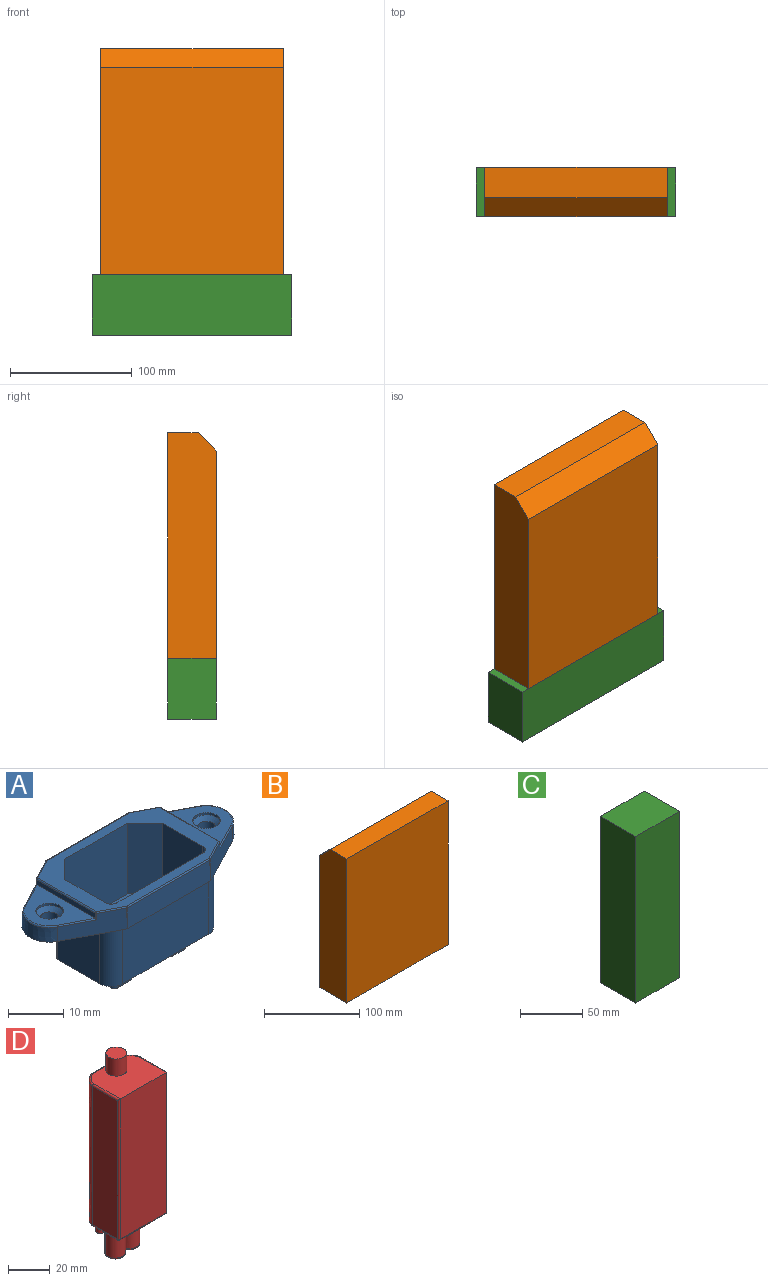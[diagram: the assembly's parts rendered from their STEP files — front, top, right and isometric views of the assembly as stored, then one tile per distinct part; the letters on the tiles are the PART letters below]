
ASSEMBLY  parts=4 mates=2
PART A: 313 faces, bbox 50.8x21.1x21.2 mm
  f0: plane 28x19.35mm, normal (0,0,-1), area 388.7mm2, adj f9,f10,f11,f12,f13,f14,f34,f35
  f1: plane 31.25x20.29mm, normal (0,0,1), area 219.7mm2, adj f15,f16,f17,f18,f19,f20,f50,f51
  f2: plane 11.73x6.18mm, normal (0.46,0.89,0.03), area 48.9mm2, adj f3,f52,f65,f67,f72,f73
  f3: cone r=5mm half-angle=2deg, axis (0,0,-1), area 33.6mm2, adj f2,f4,f52,f66
  f4: plane 11.73x6.18mm, normal (0.46,-0.89,0.03), area 48.9mm2, adj f3,f52,f68,f71,f76,f77
  f5: plane 11.73x6.18mm, normal (-0.46,-0.89,0.03), area 48.9mm2, adj f6,f52,f83,f88,f92,f94
  f6: cone r=5mm half-angle=2deg, axis (0,0,-1), area 33.6mm2, adj f5,f7,f52,f93
  f7: plane 11.73x6.18mm, normal (-0.46,0.89,0.03), area 48.9mm2, adj f6,f52,f78,f84,f89,f91
  f8: plane 25x16.35mm, normal (0,0,1), area 365.3mm2, adj f15,f16,f17,f18,f19,f20,f21,f22
  f9: plane 16.83x12.45mm, normal (0,1,0), area 209.5mm2, adj f0,f52,f108,f109
  f10: plane 12.45x5.09mm, normal (0.71,0.71,0), area 89.5mm2, adj f0,f52,f107,f108
  f11: plane 12.45x10.76mm, normal (1,0,0), area 134mm2, adj f0,f49,f52,f107
  f12: plane 22x12.45mm, normal (0,-1,0), area 273.9mm2, adj f0,f48,f49,f52
  f13: plane 12.45x10.76mm, normal (-1,0,0), area 134mm2, adj f0,f48,f52,f110
  f14: plane 12.45x5.09mm, normal (-0.71,0.71,0), area 89.5mm2, adj f0,f52,f109,f110
  f15: plane 16x15.7mm, normal (0,-1,0), area 251.2mm2, adj f1,f8,f16,f20
  f16: plane 15.7x4.5mm, normal (-0.71,-0.71,0), area 99.9mm2, adj f1,f8,f15,f17
  f17: plane 15.7x10.35mm, normal (-1,0,0), area 162.5mm2, adj f1,f8,f16,f50
  f18: plane 22x15.7mm, normal (0,1,0), area 345.4mm2, adj f1,f8,f50,f51
  f19: plane 15.7x10.35mm, normal (1,0,0), area 162.5mm2, adj f1,f8,f20,f51
  f20: plane 15.7x4.5mm, normal (0.71,-0.71,0), area 99.9mm2, adj f1,f8,f15,f19
  f21: plane 5.5x3.9mm, normal (1,0,0), area 21.5mm2, adj f8,f22,f24,f33
  f22: plane 5.5x1.9mm, normal (0,-1,0), area 10.5mm2, adj f8,f21,f23,f33
  f23: plane 5.5x3.9mm, normal (-1,0,0), area 21.5mm2, adj f8,f22,f24,f33
  f24: plane 5.5x1.9mm, normal (0,1,0), area 10.5mm2, adj f8,f21,f23,f33
  f25: plane 5.5x3.9mm, normal (1,0,0), area 21.5mm2, adj f8,f26,f28,f38
  f26: plane 5.5x1.9mm, normal (0,-1,0), area 10.5mm2, adj f8,f25,f27,f38
  f27: plane 5.5x3.9mm, normal (-1,0,0), area 21.5mm2, adj f8,f26,f28,f38
  f28: plane 5.5x1.9mm, normal (0,1,0), area 10.5mm2, adj f8,f25,f27,f38
  f29: plane 5.5x3.9mm, normal (1,0,0), area 21.5mm2, adj f8,f30,f32,f43
  f30: plane 5.5x1.9mm, normal (0,-1,0), area 10.5mm2, adj f8,f29,f31,f43
  f31: plane 5.5x3.9mm, normal (-1,0,0), area 21.5mm2, adj f8,f30,f32,f43
  f32: plane 5.5x1.9mm, normal (0,1,0), area 10.5mm2, adj f8,f29,f31,f43
  f33: plane 6.9x4.9mm, normal (0,0,-1), area 25.5mm2, adj f21,f22,f23,f24,f34,f35,f36,f37
  f34: plane 4.9x4mm, normal (1,0,0), area 19.6mm2, adj f0,f33,f95,f98
  f35: plane 4x2.9mm, normal (0,-1,0), area 11.6mm2, adj f0,f33,f95,f96
  f36: plane 4.9x4mm, normal (-1,0,0), area 19.6mm2, adj f0,f33,f96,f97
  f37: plane 4x2.9mm, normal (0,1,0), area 11.6mm2, adj f0,f33,f97,f98
  f38: plane 6.9x4.9mm, normal (0,0,-1), area 25.5mm2, adj f25,f26,f27,f28,f39,f40,f41,f42
  f39: plane 4x2.9mm, normal (0,-1,0), area 11.6mm2, adj f0,f38,f99,f102
  f40: plane 4.9x4mm, normal (-1,0,0), area 19.6mm2, adj f0,f38,f99,f100
  f41: plane 4x2.9mm, normal (0,1,0), area 11.6mm2, adj f0,f38,f100,f101
  f42: plane 4.9x4mm, normal (1,0,0), area 19.6mm2, adj f0,f38,f101,f102
  f43: plane 6.9x4.9mm, normal (0,0,-1), area 25.5mm2, adj f29,f30,f31,f32,f44,f45,f46,f47
  f44: plane 4.9x4mm, normal (1,0,0), area 19.6mm2, adj f0,f43,f104,f105
  f45: plane 4x2.9mm, normal (0,-1,0), area 11.6mm2, adj f0,f43,f103,f104
  f46: plane 4.9x4mm, normal (-1,0,0), area 19.6mm2, adj f0,f43,f103,f106
  f47: plane 4x2.9mm, normal (0,1,0), area 11.6mm2, adj f0,f43,f105,f106
  f48: cylinder r=3mm len=12.45mm, axis (0,0,1), area 58.7mm2, adj f0,f12,f13,f52
  f49: cylinder r=3mm len=12.45mm, axis (0,0,1), area 58.7mm2, adj f0,f11,f12,f52
  f50: cylinder r=1.5mm len=15.7mm, axis (0,0,-1), area 37mm2, adj f1,f8,f17,f18
  f51: cylinder r=1.5mm len=15.7mm, axis (0,0,-1), area 37mm2, adj f1,f8,f18,f19
  f52: plane 50.2x21.1mm, normal (0,0,-1), area 310mm2, adj f2,f3,f4,f5,f6,f7,f9,f10
  f53: plane 21.2x4.51mm, normal (0,1,0.03), area 95.5mm2, adj f52,f72,f78,f79
  f54: plane 21.2x4.51mm, normal (0,-1,0.03), area 95.5mm2, adj f52,f77,f82,f83
  f55: plane 15.11x1.18mm, normal (-1,0,0), area 17.3mm2, adj f56,f87,f89,f91,f92,f94
  f56: plane 14.86x8.87mm, normal (0,0,1), area 68.6mm2, adj f55,f64,f91,f93,f94
  f57: plane 14.86x8.87mm, normal (0,0,1), area 68.6mm2, adj f58,f61,f65,f66,f68
  f58: plane 15.11x1.18mm, normal (1,0,0), area 17.3mm2, adj f57,f65,f67,f68,f70,f71
  f59: cylinder r=1.65mm len=3.3mm, axis (0,0,1), area 20.7mm2, adj f52,f60
  f60: cone r=2.5mm half-angle=45deg, axis (0,0,1), area 15.7mm2, adj f59,f61
  f61: cylinder r=2.5mm len=5mm, axis (0,0,1), area 7.9mm2, adj f57,f60
  f62: cylinder r=1.65mm len=3.3mm, axis (0,0,1), area 20.7mm2, adj f52,f63
  f63: cone r=2.5mm half-angle=45deg, axis (0,0,1), area 15.7mm2, adj f62,f64
  f64: cylinder r=2.5mm len=5mm, axis (0,0,1), area 7.9mm2, adj f56,f63
  f65: cylinder r=0.25mm len=6.73mm, axis (0.89,-0.46,0), area 2.8mm2, adj f2,f57,f58,f66,f67
  f66: torus R=4.64mm, axis (0,0,1), area 4mm2, adj f3,f57,f65,f68
  f67: cylinder r=0.25mm len=1.41mm, axis (0,0.04,-1), area 0.3mm2, adj f2,f58,f65,f69
  f68: cylinder r=0.25mm len=6.73mm, axis (-0.89,-0.46,0), area 2.8mm2, adj f4,f57,f58,f66,f71
  f69: sphere r=0.25mm, area 0.1mm2, adj f67,f70,f73
  f70: cylinder r=0.25mm len=15.01mm, axis (0,1,0), area 5.9mm2, adj f1,f58,f69,f74
  f71: cylinder r=0.25mm len=1.41mm, axis (0,0.04,1), area 0.3mm2, adj f4,f58,f68,f74
  f72: cylinder r=0.25mm len=4.51mm, axis (-0.01,-0.03,1), area 0.5mm2, adj f2,f52,f53,f75
  f73: cylinder r=0.25mm len=5.18mm, axis (-0.89,0.46,0), area 2.2mm2, adj f1,f2,f69,f75
  f74: sphere r=0.25mm, area 0.1mm2, adj f70,f71,f76
  f75: sphere r=0.25mm, area 0mm2, adj f72,f73,f79
  f76: cylinder r=0.25mm len=5.18mm, axis (0.89,0.46,0), area 2.2mm2, adj f1,f4,f74,f80
  f77: cylinder r=0.25mm len=4.51mm, axis (-0.01,0.03,1), area 0.5mm2, adj f4,f52,f54,f80
  f78: cylinder r=0.25mm len=4.51mm, axis (0.01,-0.03,1), area 0.5mm2, adj f7,f52,f53,f81
  f79: cylinder r=0.25mm len=21.12mm, axis (-1,0,0), area 8.1mm2, adj f1,f53,f75,f81
  f80: sphere r=0.25mm, area 0mm2, adj f76,f77,f82
  f81: sphere r=0.25mm, area 0mm2, adj f78,f79,f84
  f82: cylinder r=0.25mm len=21.12mm, axis (1,0,0), area 8.1mm2, adj f1,f54,f80,f85
  f83: cylinder r=0.25mm len=4.51mm, axis (0.01,0.03,1), area 0.5mm2, adj f5,f52,f54,f85
  f84: cylinder r=0.25mm len=5.18mm, axis (-0.89,-0.46,0), area 2.2mm2, adj f1,f7,f81,f86
  f85: sphere r=0.25mm, area 0mm2, adj f82,f83,f88
  f86: sphere r=0.25mm, area 0.1mm2, adj f84,f87,f89
  f87: cylinder r=0.25mm len=15.01mm, axis (0,-1,0), area 5.9mm2, adj f1,f55,f86,f90
  f88: cylinder r=0.25mm len=5.18mm, axis (0.89,-0.46,0), area 2.2mm2, adj f1,f5,f85,f90
  f89: cylinder r=0.25mm len=1.41mm, axis (0,-0.04,1), area 0.3mm2, adj f7,f55,f86,f91
  f90: sphere r=0.25mm, area 0.1mm2, adj f87,f88,f92
  f91: cylinder r=0.25mm len=6.73mm, axis (0.89,0.46,0), area 2.8mm2, adj f7,f55,f56,f89,f93
  f92: cylinder r=0.25mm len=1.41mm, axis (0,-0.04,-1), area 0.3mm2, adj f5,f55,f90,f94
  f93: torus R=4.64mm, axis (0,0,1), area 4mm2, adj f6,f56,f91,f94
  f94: cylinder r=0.25mm len=6.73mm, axis (-0.89,0.46,0), area 2.8mm2, adj f5,f55,f56,f92,f93
  f95: cylinder r=1mm len=4mm, axis (0,0,1), area 6.3mm2, adj f0,f33,f34,f35
  f96: cylinder r=1mm len=4mm, axis (0,0,1), area 6.3mm2, adj f0,f33,f35,f36
  f97: cylinder r=1mm len=4mm, axis (0,0,1), area 6.3mm2, adj f0,f33,f36,f37
  f98: cylinder r=1mm len=4mm, axis (0,0,1), area 6.3mm2, adj f0,f33,f34,f37
  f99: cylinder r=1mm len=4mm, axis (0,0,1), area 6.3mm2, adj f0,f38,f39,f40
  f100: cylinder r=1mm len=4mm, axis (0,0,1), area 6.3mm2, adj f0,f38,f40,f41
  f101: cylinder r=1mm len=4mm, axis (0,0,1), area 6.3mm2, adj f0,f38,f41,f42
  f102: cylinder r=1mm len=4mm, axis (0,0,1), area 6.3mm2, adj f0,f38,f39,f42
  f103: cylinder r=1mm len=4mm, axis (0,0,1), area 6.3mm2, adj f0,f43,f45,f46
  f104: cylinder r=1mm len=4mm, axis (0,0,1), area 6.3mm2, adj f0,f43,f44,f45
  f105: cylinder r=1mm len=4mm, axis (0,0,1), area 6.3mm2, adj f0,f43,f44,f47
  f106: cylinder r=1mm len=4mm, axis (0,0,1), area 6.3mm2, adj f0,f43,f46,f47
  f107: cylinder r=0.5mm len=12.45mm, axis (0,0,1), area 4.9mm2, adj f0,f10,f11,f52
  f108: cylinder r=0.5mm len=12.45mm, axis (0,0,1), area 4.9mm2, adj f0,f9,f10,f52
  f109: cylinder r=0.5mm len=12.45mm, axis (0,0,1), area 4.9mm2, adj f0,f9,f14,f52
  f110: cylinder r=0.5mm len=12.45mm, axis (0,0,1), area 4.9mm2, adj f0,f13,f14,f52
  f111: plane 2x0.2mm, normal (-1,0,0), area 0.4mm2, adj f0,f112,f117,f118
  f112: plane 0.2x0.17mm, normal (0,1,0), area 0mm2, adj f0,f111,f113,f118
  f113: extruded ~0.55x0.5mm, area 0.2mm2, adj f0,f112,f114,f118
  f114: plane 0.24x0.2mm, normal (1,0,0), area 0mm2, adj f0,f113,f115,f118
  f115: extruded ~0.46x0.3mm, area 0.1mm2, adj f0,f114,f116,f118
  f116: plane 1.56x0.2mm, normal (1,0,0), area 0.3mm2, adj f0,f115,f117,f118
  f117: plane 0.26x0.2mm, normal (0,-1,0), area 0.1mm2, adj f0,f111,f116,f118
  f118: plane 2x0.72mm, normal (0,0,-1), area 0.6mm2, adj f111,f112,f113,f114,f115,f116,f117
  f119: plane 2.03x1.28mm, normal (0,0,-1), area 1.2mm2, adj f120,f121,f122,f123,f124,f125,f126,f127
  f120: extruded ~0.82x0.2mm, area 0.2mm2, adj f0,f119,f121,f124
  f121: extruded ~0.45x0.2mm, area 0.1mm2, adj f0,f119,f120,f122
  f122: extruded ~1.01x0.64mm, area 0.3mm2, adj f0,f119,f121,f123
  f123: extruded ~1.01x0.64mm, area 0.3mm2, adj f0,f119,f122,f124
  f124: extruded ~1.01x0.64mm, area 0.3mm2, adj f0,f119,f120,f123
  f125: extruded ~0.65x0.2mm, area 0.1mm2, adj f119,f126,f129,f130
  f126: extruded ~0.78x0.38mm, area 0.2mm2, adj f119,f125,f127,f130
  f127: extruded ~0.78x0.38mm, area 0.2mm2, adj f119,f126,f128,f130
  f128: extruded ~0.78x0.39mm, area 0.2mm2, adj f119,f127,f129,f130
  f129: extruded ~0.27x0.2mm, area 0.1mm2, adj f119,f125,f128,f130
  f130: plane 1.56x0.77mm, normal (0,0,-1), area 1mm2, adj f125,f126,f127,f128,f129
  f131: plane 2x1.91mm, normal (0,0,-1), area 1.2mm2, adj f132,f133,f134,f135,f136,f137,f138,f139
  f132: plane 0.3x0.2mm, normal (0,-1,0), area 0.1mm2, adj f0,f131,f133,f139
  f133: plane 0.62x0.23mm, normal (-0.94,-0.35,0), area 0.1mm2, adj f0,f131,f132,f134
  f134: plane 0.85x0.2mm, normal (0,-1,0), area 0.2mm2, adj f0,f131,f133,f135
  f135: plane 0.62x0.23mm, normal (0.94,-0.35,0), area 0.1mm2, adj f0,f131,f134,f136
  f136: plane 0.3x0.2mm, normal (0,-1,0), area 0.1mm2, adj f0,f131,f135,f137
  f137: plane 2x0.79mm, normal (-0.93,0.37,0), area 0.4mm2, adj f0,f131,f136,f138
  f138: plane 0.32x0.2mm, normal (0,1,0), area 0.1mm2, adj f0,f131,f137,f139
  f139: plane 2x0.79mm, normal (0.93,0.37,0), area 0.4mm2, adj f0,f131,f132,f138
  f140: plane 0.55x0.2mm, normal (-0.94,-0.35,0), area 0.1mm2, adj f131,f141,f144,f145
  f141: plane 0.68x0.2mm, normal (0,1,0), area 0.1mm2, adj f131,f140,f142,f145
  f142: plane 0.53x0.2mm, normal (0.94,-0.35,0), area 0.1mm2, adj f131,f141,f143,f145
  f143: extruded ~0.4x0.2mm, area 0.1mm2, adj f131,f142,f144,f145
  f144: extruded ~0.37x0.2mm, area 0.1mm2, adj f131,f140,f143,f145
  f145: plane 0.92x0.68mm, normal (0,0,-1), area 0.3mm2, adj f140,f141,f142,f143,f144
  f146: extruded ~0.35x0.23mm, area 0.1mm2, adj f0,f147,f154,f155
  f147: extruded ~0.66x0.23mm, area 0.1mm2, adj f0,f146,f148,f155
  f148: extruded ~0.38x0.23mm, area 0.1mm2, adj f0,f147,f149,f155
  f149: plane 0.28x0.2mm, normal (-1,0,0), area 0.1mm2, adj f0,f148,f150,f155
  f150: extruded ~0.35x0.23mm, area 0.1mm2, adj f0,f149,f151,f155
  f151: extruded ~0.23x0.2mm, area 0.1mm2, adj f0,f150,f152,f155
  f152: extruded ~0.43x0.2mm, area 0.1mm2, adj f0,f151,f153,f155
  f153: extruded ~0.38x0.23mm, area 0.1mm2, adj f0,f152,f154,f155
  f154: plane 0.28x0.2mm, normal (1,0,0), area 0.1mm2, adj f0,f146,f153,f155
  f155: plane 1.38x0.51mm, normal (0,0,-1), area 0.4mm2, adj f146,f147,f148,f149,f150,f151,f152,f153
  f156: plane 2x0.2mm, normal (-1,0,0), area 0.4mm2, adj f0,f157,f162,f163
  f157: plane 0.2x0.17mm, normal (0,1,0), area 0mm2, adj f0,f156,f158,f163
  f158: extruded ~0.55x0.5mm, area 0.2mm2, adj f0,f157,f159,f163
  f159: plane 0.24x0.2mm, normal (1,0,0), area 0mm2, adj f0,f158,f160,f163
  f160: extruded ~0.46x0.3mm, area 0.1mm2, adj f0,f159,f161,f163
  f161: plane 1.56x0.2mm, normal (1,0,0), area 0.3mm2, adj f0,f160,f162,f163
  f162: plane 0.26x0.2mm, normal (0,-1,0), area 0.1mm2, adj f0,f156,f161,f163
  f163: plane 2x0.72mm, normal (0,0,-1), area 0.6mm2, adj f156,f157,f158,f159,f160,f161,f162
  f164: extruded ~0.62x0.56mm, area 0.2mm2, adj f0,f165,f179,f180
  f165: extruded ~0.51x0.24mm, area 0.1mm2, adj f0,f164,f166,f180
  f166: extruded ~0.47x0.2mm, area 0.1mm2, adj f0,f165,f167,f180
  f167: extruded ~0.65x0.59mm, area 0.2mm2, adj f0,f166,f168,f180
  f168: extruded ~0.36x0.2mm, area 0.1mm2, adj f0,f167,f169,f180
  f169: plane 0.52x0.2mm, normal (-0.98,-0.19,0), area 0.1mm2, adj f0,f168,f170,f180
  f170: plane 0.74x0.2mm, normal (0,-1,0), area 0.1mm2, adj f0,f169,f171,f180
  f171: plane 0.26x0.2mm, normal (-1,0,0), area 0.1mm2, adj f0,f170,f172,f180
  f172: plane 0.95x0.2mm, normal (0,1,0), area 0.2mm2, adj f0,f171,f173,f180
  f173: plane 1.03x0.21mm, normal (0.98,0.2,0), area 0.2mm2, adj f0,f172,f174,f180
  f174: plane 0.26x0.2mm, normal (0.1,-1,0), area 0.1mm2, adj f0,f173,f175,f180
  f175: extruded ~0.34x0.2mm, area 0.1mm2, adj f0,f174,f176,f180
  f176: extruded ~0.43x0.4mm, area 0.1mm2, adj f0,f175,f177,f180
  f177: extruded ~0.47x0.4mm, area 0.1mm2, adj f0,f176,f178,f180
  f178: extruded ~0.37x0.36mm, area 0.1mm2, adj f0,f177,f179,f180
  f179: plane 0.26x0.2mm, normal (0.1,1,0), area 0.1mm2, adj f0,f164,f178,f180
  f180: plane 2x1.28mm, normal (0,0,-1), area 1.1mm2, adj f164,f165,f166,f167,f168,f169,f170,f171
  f181: plane 2x1.91mm, normal (0,0,-1), area 1.2mm2, adj f182,f183,f184,f185,f186,f187,f188,f189
  f182: plane 0.3x0.2mm, normal (0,-1,0), area 0.1mm2, adj f0,f181,f183,f189
  f183: plane 0.62x0.23mm, normal (-0.94,-0.35,0), area 0.1mm2, adj f0,f181,f182,f184
  f184: plane 0.85x0.2mm, normal (0,-1,0), area 0.2mm2, adj f0,f181,f183,f185
  f185: plane 0.62x0.23mm, normal (0.94,-0.35,0), area 0.1mm2, adj f0,f181,f184,f186
  f186: plane 0.3x0.2mm, normal (0,-1,0), area 0.1mm2, adj f0,f181,f185,f187
  f187: plane 2x0.79mm, normal (-0.93,0.37,0), area 0.4mm2, adj f0,f181,f186,f188
  f188: plane 0.32x0.2mm, normal (0,1,0), area 0.1mm2, adj f0,f181,f187,f189
  f189: plane 2x0.79mm, normal (0.93,0.37,0), area 0.4mm2, adj f0,f181,f182,f188
  f190: plane 0.55x0.2mm, normal (-0.94,-0.35,0), area 0.1mm2, adj f181,f191,f194,f195
  f191: plane 0.68x0.2mm, normal (0,1,0), area 0.1mm2, adj f181,f190,f192,f195
  f192: plane 0.53x0.2mm, normal (0.94,-0.35,0), area 0.1mm2, adj f181,f191,f193,f195
  f193: extruded ~0.4x0.2mm, area 0.1mm2, adj f181,f192,f194,f195
  f194: extruded ~0.37x0.2mm, area 0.1mm2, adj f181,f190,f193,f195
  f195: plane 0.92x0.68mm, normal (0,0,-1), area 0.3mm2, adj f190,f191,f192,f193,f194
  f196: plane 2x0.2mm, normal (-1,0,0), area 0.4mm2, adj f0,f197,f202,f203
  f197: plane 0.2x0.17mm, normal (0,1,0), area 0mm2, adj f0,f196,f198,f203
  f198: extruded ~0.55x0.5mm, area 0.2mm2, adj f0,f197,f199,f203
  f199: plane 0.24x0.2mm, normal (1,0,0), area 0mm2, adj f0,f198,f200,f203
  f200: extruded ~0.46x0.3mm, area 0.1mm2, adj f0,f199,f201,f203
  f201: plane 1.56x0.2mm, normal (1,0,0), area 0.3mm2, adj f0,f200,f202,f203
  f202: plane 0.26x0.2mm, normal (0,-1,0), area 0.1mm2, adj f0,f196,f201,f203
  f203: plane 2x0.72mm, normal (0,0,-1), area 0.6mm2, adj f196,f197,f198,f199,f200,f201,f202
  f204: plane 2.03x1.28mm, normal (0,0,-1), area 1.2mm2, adj f205,f206,f207,f208,f209,f210,f211,f212
  f205: extruded ~0.82x0.2mm, area 0.2mm2, adj f0,f204,f206,f209
  f206: extruded ~0.45x0.2mm, area 0.1mm2, adj f0,f204,f205,f207
  f207: extruded ~1.01x0.64mm, area 0.3mm2, adj f0,f204,f206,f208
  f208: extruded ~1.01x0.64mm, area 0.3mm2, adj f0,f204,f207,f209
  f209: extruded ~1.01x0.64mm, area 0.3mm2, adj f0,f204,f205,f208
  f210: extruded ~0.65x0.2mm, area 0.1mm2, adj f204,f211,f214,f215
  f211: extruded ~0.78x0.38mm, area 0.2mm2, adj f204,f210,f212,f215
  f212: extruded ~0.78x0.38mm, area 0.2mm2, adj f204,f211,f213,f215
  f213: extruded ~0.78x0.39mm, area 0.2mm2, adj f204,f212,f214,f215
  f214: extruded ~0.27x0.2mm, area 0.1mm2, adj f204,f210,f213,f215
  f215: plane 1.56x0.77mm, normal (0,0,-1), area 1mm2, adj f210,f211,f212,f213,f214
  f216: plane 2x1.91mm, normal (0,0,-1), area 1.2mm2, adj f217,f218,f219,f220,f221,f222,f223,f224
  f217: plane 0.3x0.2mm, normal (0,-1,0), area 0.1mm2, adj f0,f216,f218,f224
  f218: plane 0.62x0.23mm, normal (-0.94,-0.35,0), area 0.1mm2, adj f0,f216,f217,f219
  f219: plane 0.85x0.2mm, normal (0,-1,0), area 0.2mm2, adj f0,f216,f218,f220
  f220: plane 0.62x0.23mm, normal (0.94,-0.35,0), area 0.1mm2, adj f0,f216,f219,f221
  f221: plane 0.3x0.2mm, normal (0,-1,0), area 0.1mm2, adj f0,f216,f220,f222
  f222: plane 2x0.79mm, normal (-0.93,0.37,0), area 0.4mm2, adj f0,f216,f221,f223
  f223: plane 0.32x0.2mm, normal (0,1,0), area 0.1mm2, adj f0,f216,f222,f224
  f224: plane 2x0.79mm, normal (0.93,0.37,0), area 0.4mm2, adj f0,f216,f217,f223
  f225: plane 0.55x0.2mm, normal (-0.94,-0.35,0), area 0.1mm2, adj f216,f226,f229,f230
  f226: plane 0.68x0.2mm, normal (0,1,0), area 0.1mm2, adj f216,f225,f227,f230
  f227: plane 0.53x0.2mm, normal (0.94,-0.35,0), area 0.1mm2, adj f216,f226,f228,f230
  f228: extruded ~0.4x0.2mm, area 0.1mm2, adj f216,f227,f229,f230
  f229: extruded ~0.37x0.2mm, area 0.1mm2, adj f216,f225,f228,f230
  f230: plane 0.92x0.68mm, normal (0,0,-1), area 0.3mm2, adj f225,f226,f227,f228,f229
  f231: plane 0.98x0.2mm, normal (0,1,0), area 0.2mm2, adj f0,f232,f243,f244
  f232: extruded ~0.4x0.37mm, area 0.1mm2, adj f0,f231,f233,f244
  f233: extruded ~0.82x0.56mm, area 0.2mm2, adj f0,f232,f234,f244
  f234: extruded ~0.62x0.55mm, area 0.2mm2, adj f0,f233,f235,f244
  f235: extruded ~0.64x0.56mm, area 0.2mm2, adj f0,f234,f236,f244
  f236: plane 0.26x0.2mm, normal (0.1,-1,0), area 0.1mm2, adj f0,f235,f237,f244
  f237: extruded ~0.38x0.36mm, area 0.1mm2, adj f0,f236,f238,f244
  f238: extruded ~0.36x0.32mm, area 0.1mm2, adj f0,f237,f239,f244
  f239: extruded ~0.7x0.54mm, area 0.2mm2, adj f0,f238,f240,f244
  f240: extruded ~0.57x0.46mm, area 0.1mm2, adj f0,f239,f241,f244
  f241: extruded ~0.2x0.18mm, area 0mm2, adj f0,f240,f242,f244
  f242: plane 1.31x0.2mm, normal (0,-1,0), area 0.3mm2, adj f0,f241,f243,f244
  f243: plane 0.26x0.2mm, normal (-1,0,0), area 0.1mm2, adj f0,f231,f242,f244
  f244: plane 2x1.31mm, normal (0,0,-1), area 1.1mm2, adj f231,f232,f233,f234,f235,f236,f237,f238
  f245: extruded ~0.62x0.56mm, area 0.2mm2, adj f0,f246,f260,f261
  f246: extruded ~0.51x0.24mm, area 0.1mm2, adj f0,f245,f247,f261
  f247: extruded ~0.47x0.2mm, area 0.1mm2, adj f0,f246,f248,f261
  f248: extruded ~0.65x0.59mm, area 0.2mm2, adj f0,f247,f249,f261
  f249: extruded ~0.36x0.2mm, area 0.1mm2, adj f0,f248,f250,f261
  f250: plane 0.52x0.2mm, normal (-0.98,-0.19,0), area 0.1mm2, adj f0,f249,f251,f261
  f251: plane 0.74x0.2mm, normal (0,-1,0), area 0.1mm2, adj f0,f250,f252,f261
  f252: plane 0.26x0.2mm, normal (-1,0,0), area 0.1mm2, adj f0,f251,f253,f261
  f253: plane 0.95x0.2mm, normal (0,1,0), area 0.2mm2, adj f0,f252,f254,f261
  f254: plane 1.03x0.21mm, normal (0.98,0.2,0), area 0.2mm2, adj f0,f253,f255,f261
  f255: plane 0.26x0.2mm, normal (0.1,-1,0), area 0.1mm2, adj f0,f254,f256,f261
  f256: extruded ~0.34x0.2mm, area 0.1mm2, adj f0,f255,f257,f261
  f257: extruded ~0.43x0.4mm, area 0.1mm2, adj f0,f256,f258,f261
  f258: extruded ~0.47x0.4mm, area 0.1mm2, adj f0,f257,f259,f261
  f259: extruded ~0.37x0.36mm, area 0.1mm2, adj f0,f258,f260,f261
  f260: plane 0.26x0.2mm, normal (0.1,1,0), area 0.1mm2, adj f0,f245,f259,f261
  f261: plane 2x1.28mm, normal (0,0,-1), area 1.1mm2, adj f245,f246,f247,f248,f249,f250,f251,f252
  f262: plane 2.03x1.28mm, normal (0,0,-1), area 1.2mm2, adj f263,f264,f265,f266,f267,f268,f269,f270
  f263: extruded ~0.82x0.2mm, area 0.2mm2, adj f0,f262,f264,f267
  f264: extruded ~0.45x0.2mm, area 0.1mm2, adj f0,f262,f263,f265
  f265: extruded ~1.01x0.64mm, area 0.3mm2, adj f0,f262,f264,f266
  f266: extruded ~1.01x0.64mm, area 0.3mm2, adj f0,f262,f265,f267
  f267: extruded ~1.01x0.64mm, area 0.3mm2, adj f0,f262,f263,f266
  f268: extruded ~0.65x0.2mm, area 0.1mm2, adj f262,f269,f272,f273
  f269: extruded ~0.78x0.38mm, area 0.2mm2, adj f262,f268,f270,f273
  f270: extruded ~0.78x0.38mm, area 0.2mm2, adj f262,f269,f271,f273
  f271: extruded ~0.78x0.39mm, area 0.2mm2, adj f262,f270,f272,f273
  f272: extruded ~0.27x0.2mm, area 0.1mm2, adj f262,f268,f271,f273
  f273: plane 1.56x0.77mm, normal (0,0,-1), area 1mm2, adj f268,f269,f270,f271,f272
  f274: plane 0.31x0.2mm, normal (0,-1,0), area 0.1mm2, adj f0,f275,f282,f283
  f275: plane 2x0.81mm, normal (-0.93,-0.37,0), area 0.4mm2, adj f0,f274,f276,f283
  f276: plane 0.31x0.2mm, normal (0,1,0), area 0.1mm2, adj f0,f275,f277,f283
  f277: plane 1.43x0.55mm, normal (0.93,0.36,0), area 0.3mm2, adj f0,f276,f278,f283
  f278: extruded ~0.32x0.2mm, area 0.1mm2, adj f0,f277,f279,f283
  f279: extruded ~0.32x0.2mm, area 0.1mm2, adj f0,f278,f280,f283
  f280: plane 1.43x0.54mm, normal (-0.93,0.35,0), area 0.3mm2, adj f0,f279,f281,f283
  f281: plane 0.31x0.2mm, normal (0,1,0), area 0.1mm2, adj f0,f280,f282,f283
  f282: plane 2x0.81mm, normal (0.93,-0.37,0), area 0.4mm2, adj f0,f274,f281,f283
  f283: plane 2x1.92mm, normal (0,0,-1), area 1.1mm2, adj f274,f275,f276,f277,f278,f279,f280,f281
  f284: plane 0.28x0.2mm, normal (0,-1,0), area 0.1mm2, adj f0,f285,f293,f294
  f285: plane 0.9x0.2mm, normal (-1,0,0), area 0.2mm2, adj f0,f284,f286,f294
  f286: plane 0.9x0.2mm, normal (0,-1,0), area 0.2mm2, adj f0,f285,f287,f294
  f287: plane 0.23x0.2mm, normal (-1,0,0), area 0mm2, adj f0,f286,f288,f294
  f288: plane 0.9x0.2mm, normal (0,1,0), area 0.2mm2, adj f0,f287,f289,f294
  f289: plane 0.64x0.2mm, normal (-1,0,0), area 0.1mm2, adj f0,f288,f290,f294
  f290: plane 1.05x0.2mm, normal (0,-1,0), area 0.2mm2, adj f0,f289,f291,f294
  f291: plane 0.23x0.2mm, normal (-1,0,0), area 0mm2, adj f0,f290,f292,f294
  f292: plane 1.33x0.2mm, normal (0,1,0), area 0.3mm2, adj f0,f291,f293,f294
  f293: plane 2x0.2mm, normal (1,0,0), area 0.4mm2, adj f0,f284,f292,f294
  f294: plane 2x1.33mm, normal (0,0,-1), area 1mm2, adj f284,f285,f286,f287,f288,f289,f290,f291
  f295: plane 0.28x0.2mm, normal (0,-1,0), area 0.1mm2, adj f0,f296,f304,f305
  f296: plane 1.49x0.2mm, normal (-1,0,0), area 0.3mm2, adj f0,f295,f297,f305
  f297: plane 1.49x0.96mm, normal (0.84,-0.54,0), area 0.4mm2, adj f0,f296,f298,f305
  f298: plane 0.3x0.2mm, normal (0,-1,0), area 0.1mm2, adj f0,f297,f299,f305
  f299: plane 2x0.2mm, normal (-1,0,0), area 0.4mm2, adj f0,f298,f300,f305
  f300: plane 0.28x0.2mm, normal (0,1,0), area 0.1mm2, adj f0,f299,f301,f305
  f301: plane 1.49x0.2mm, normal (1,0,0), area 0.3mm2, adj f0,f300,f302,f305
  f302: plane 1.49x0.96mm, normal (-0.84,0.54,0), area 0.4mm2, adj f0,f301,f303,f305
  f303: plane 0.3x0.2mm, normal (0,1,0), area 0.1mm2, adj f0,f302,f304,f305
  f304: plane 2x0.2mm, normal (1,0,0), area 0.4mm2, adj f0,f295,f303,f305
  f305: plane 2x1.54mm, normal (0,0,-1), area 1.6mm2, adj f295,f296,f297,f298,f299,f300,f301,f302
  f306: plane 1.23x0.2mm, normal (0,-1,0), area 0.2mm2, adj f0,f307,f311,f312
  f307: plane 0.23x0.2mm, normal (-1,0,0), area 0mm2, adj f0,f306,f308,f312
  f308: plane 0.95x0.2mm, normal (0,1,0), area 0.2mm2, adj f0,f307,f309,f312
  f309: plane 1.77x0.2mm, normal (-1,0,0), area 0.4mm2, adj f0,f308,f310,f312
  f310: plane 0.28x0.2mm, normal (0,1,0), area 0.1mm2, adj f0,f309,f311,f312
  f311: plane 2x0.2mm, normal (1,0,0), area 0.4mm2, adj f0,f306,f310,f312
  f312: plane 2x1.23mm, normal (0,0,-1), area 0.8mm2, adj f306,f307,f308,f309,f310,f311
PART B: 7 faces, bbox 150x40x185 mm
  f0: plane 150x40mm, normal (0,0,-1), area 6000mm2, adj f1,f3,f4,f5
  f1: plane 185x40mm, normal (1,0,0), area 7287.5mm2, adj f0,f2,f4,f5,f6
  f2: plane 150x25mm, normal (0,0,1), area 3750mm2, adj f1,f3,f4,f6
  f3: plane 185x40mm, normal (-1,0,0), area 7287.5mm2, adj f0,f2,f4,f5,f6
  f4: plane 185x150mm, normal (0,-1,0), area 27750mm2, adj f0,f1,f2,f3
  f5: plane 170x150mm, normal (0,1,0), area 25500mm2, adj f0,f1,f3,f6
  f6: plane 150x15mm, normal (0,0.71,0.71), area 3182mm2, adj f1,f2,f3,f5
PART C: 6 faces, bbox 50x40x164 mm
  f0: plane 164x40mm, normal (1,0,0), area 6560mm2, adj f1,f3,f4,f5
  f1: plane 50x40mm, normal (0,0,1), area 2000mm2, adj f0,f2,f3,f4
  f2: plane 164x40mm, normal (-1,0,0), area 6560mm2, adj f1,f3,f4,f5
  f3: plane 164x50mm, normal (0,-1,0), area 8200mm2, adj f0,f1,f2,f5
  f4: plane 164x50mm, normal (0,1,0), area 8200mm2, adj f0,f1,f2,f5
  f5: plane 50x40mm, normal (0,0,-1), area 2000mm2, adj f0,f2,f3,f4
PART D: 42 faces, bbox 33x25x113 mm
  f0: cylinder r=5mm len=18mm, axis (0,0,1), area 554.7mm2, adj f17,f18,f36,f39
  f1: plane 31x23mm, normal (0,0,-1), area 426.1mm2, adj f19,f20,f21,f24,f26,f27,f34,f36
  f2: plane 81x17mm, normal (1,0,0), area 1377mm2, adj f11,f20,f22,f25
  f3: plane 31x24mm, normal (0,0,1), area 644.4mm2, adj f5,f13,f25,f28,f30,f32,f33
  f4: plane 81x17mm, normal (-1,0,0), area 1377mm2, adj f12,f27,f31,f33
  f5: plane 82x31mm, normal (0,-1,0), area 2542mm2, adj f3,f22,f26,f31
  f6: plane 81x19mm, normal (0,1,0), area 1539mm2, adj f11,f12,f21,f30
  f7: cylinder r=2.45mm len=18mm, axis (0,0,1), area 19.5mm2, adj f8,f35,f41
  f8: cylinder r=5mm len=18mm, axis (0,0,1), area 546.1mm2, adj f7,f37,f40
  f9: plane 8x8mm, normal (0,0,-1), area 50.2mm2, adj f40,f41
  f10: plane 8x8mm, normal (0,0,-1), area 50.3mm2, adj f39
  f11: bspline ~91.3x7mm, area 855.6mm2, adj f2,f6,f19,f28
  f12: bspline ~91.3x7mm, area 855.6mm2, adj f4,f6,f24,f32
  f13: cylinder r=4.99mm len=10mm, axis (0,0,-1), area 313.3mm2, adj f3,f14
  f14: plane 9.97x9.97mm, normal (0,0,1), area 78.1mm2, adj f13
  f15: cylinder r=2.18mm len=4.36mm, axis (0,0,1), area 54.8mm2, adj f16,f38
  f16: plane 4.36x4.36mm, normal (0,0,-1), area 14.9mm2, adj f15
  f17: cylinder r=2.18mm len=4.36mm, axis (0,0,1), area 43.4mm2, adj f0,f18,f34
  f18: plane 4.36x4.3mm, normal (0,0,-1), area 13.8mm2, adj f0,f17
  f19: bspline ~8.05x7.35mm, area 15.7mm2, adj f1,f11,f20,f21
  f20: cylinder r=1mm len=17mm, axis (0,1,0), area 26.7mm2, adj f1,f2,f19,f23
  f21: cylinder r=1mm len=19mm, axis (1,0,0), area 29.8mm2, adj f1,f6,f19,f24
  f22: cylinder r=1mm len=82mm, axis (0,0,-1), area 128mm2, adj f2,f5,f23,f25
  f23: sphere r=1mm, area 1.6mm2, adj f20,f22,f26
  f24: bspline ~8.05x7.35mm, area 15.7mm2, adj f1,f12,f21,f27
  f25: cylinder r=1mm len=18mm, axis (0,-1,0), area 27.5mm2, adj f2,f3,f22,f28
  f26: cylinder r=1mm len=31mm, axis (-1,0,0), area 48.7mm2, adj f1,f5,f23,f29
  f27: cylinder r=1mm len=17mm, axis (0,-1,0), area 26.7mm2, adj f1,f4,f24,f29
  f28: bspline ~8.05x7.35mm, area 15.7mm2, adj f3,f11,f25,f30
  f29: sphere r=1mm, area 1.6mm2, adj f26,f27,f31
  f30: cylinder r=1mm len=19mm, axis (-1,0,0), area 29.8mm2, adj f3,f6,f28,f32
  f31: cylinder r=1mm len=82mm, axis (0,0,1), area 128mm2, adj f4,f5,f29,f33
  f32: bspline ~8.05x7.35mm, area 15.7mm2, adj f3,f12,f30,f33
  f33: cylinder r=1mm len=18mm, axis (0,1,0), area 27.5mm2, adj f3,f4,f31,f32
  f34: torus R=3.18mm, axis (0,0,-1), area 17.8mm2, adj f1,f17,f36
  f35: torus R=1.45mm, axis (0,0,-1), area 0.6mm2, adj f7,f37,f38
  f36: torus R=6mm, axis (0,0,-1), area 42.3mm2, adj f0,f1,f34,f37
  f37: torus R=6mm, axis (0,0,-1), area 45.2mm2, adj f1,f8,f35,f36,f38
  f38: torus R=3.18mm, axis (0,0,-1), area 21.8mm2, adj f1,f15,f35,f37
  f39: torus R=4mm, axis (0,0,-1), area 45.8mm2, adj f0,f10
  f40: torus R=4mm, axis (0,0,-1), area 43.9mm2, adj f8,f9,f41
  f41: torus R=3.45mm, axis (0,0,-1), area 1.7mm2, adj f7,f9,f40
PLACE A t=(44.73,3.69,6.33)mm
PLACE B rot(axis=(0,0,1),180deg) t=(89.73,-15.69,94.08)mm
PLACE C rot(axis=(0,1,0),90deg) t=(89.73,24.31,-28.6)mm
PLACE D rot(axis=(0,-1,0),90deg) t=(60.54,11.81,-22.03)mm
MATE fastened B.f0 <-> C.f2  axis (0,0,-1) through (89.73,4.31,1.58)mm
MATE fastened C.f2 <-> A.f52  axis (0,0,1) through (89.73,4.31,1.58)mm
